# Revit family: HUNTER_PROS-04_PRS40
name_source: partatom
category: Sprinklers
revit_build: Autodesk Revit 2017 (Build: 20160225_1515(x64)
units: mm (PartAtom-declared; Revit-internal decimal feet)

## family parameters
Always vertical = Yes
Cut with Voids When Loaded = No
Maintain Annotation Orientation = No
OmniClass Number = 23.11.27.15.11.11
OmniClass Title = Installed Sprinkler Heads
Part Type = Normal
Room Calculation Point = No
Round Connector Dimension = Use Diameter
Shared = Yes
Work Plane-Based = No

## types (19) — shared parameters
Assembly Code = G2050700
Body Height = 155 mm  [stored 0.50853 ft]
Body Material = Hunter® ABS Plastic
Connection_Dia = 15 mm  [stored 0.0492126 ft]
Diameter = 610 mm
Exposed Diameter = 57 mm  [stored 0.187008 ft]
Keynote = 328423.02
Manufacturer = Hunter® Industries
Pop Up Height = 100 mm  [stored 0.328084 ft]
Pop Up Material = Hunter® ABS Plastic
Pressure = 280.0 kPa
Seal = Hunter® White Flex Seal
Trajectory Angle = 25.00°
Type Comments = Pro-Spray® PROS-04
Type Image = <None>
URL = https://www.hunterindustries.com
Water = Water

## per-type parameters (varying)
| type | Arc Max | Arc Min | Description | Inlet Size | MP_Ref_1 | MP_Ref_2 | Model | Nozzle Size | Precipitation Rate | Trajectory Radius | Water Pattern |
| PROS-04-PRS40-CV-MP1000-90_Maroon_4.1m | 210.00° | 90.00° | ProSpray® with Pressure Regulator PROS-04-PRS40 10cm PopUp and MP Rotator MP1000-90 | 1/2'' NPT | 1000 | 90 | PROS-04-PRS40-CV-MP1000-90 | Hunter®MP Rotator (MP1000) Maroon Nozzle | 11 mm/hr | 4100 mm  [stored 13.4514 ft] | Water Arc |
| PROS-04-PRS40-CV-MP1000-360_Olive_4.1m | 360.00° | 360.00° | ProSpray® with Pressure Regulator PROS-04-PRS40 10cm PopUp and MP Rotator MP1000-360 | 1/2" NPT | 1000 | 360 | PROS-04-PRS40-CV-MP1000-360 | Hunter®MP Rotator (MP1000) Olive Nozzle | 11 mm/hr | 4100 mm  [stored 13.4514 ft] | Water Arc |
| PROS-04-PRS40-CV-MP1000-210_Lt.Blue_4.1m | 270.00° | 210.00° | ProSpray® with Pressure Regulator PROS-04-PRS40 10cm PopUp and MP Rotator MP1000-210 | 1/2" NPT | 1000 | 210 | PROS-04-PRS40-CV-MP1000-210 | Hunter® MP Rotator (MP1000) Lt.Blue Nozzle | 11 mm/hr | 4100 mm  [stored 13.4514 ft] | Water Arc |
| PROS-04-PRS40-CV-MP2000-210_Green_5.8 m | 270.00° | 210.00° | ProSpray® with Pressure Regulator PROS-04-PRS40 10cm PopUp and MP Rotator MP2000-210 | 1/2" NPT | 2000 | 210 | PROS-04-PRS40-CV-MP2000-210 | Hunter® MP Rotator (MP2000) Green Nozzle | 10 mm/hr | 5800 mm  [stored 19.0289 ft] | Water Arc |
| PROS-04-PRS40-CV-MP2000-90_Black_5.8m | 210.00° | 90.00° | ProSpray® with Pressure Regulator PROS-04-PRS40 10cm PopUp and MP Rotator MP2000-90 | 1/2'' NPT | 2000 | 90 | PROS-04-PRS40-CV-MP2000-90 | Hunter® MP Rotator (MP2000) Black Nozzle | 11 mm/hr | 5800 mm  [stored 19.0289 ft] | Water Arc |
| PROS-04-PRS40-CV-MP2000-360_Red_5.8m | 360.00° | 360.00° | ProSpray® with Pressure Regulator PROS-04-PRS40 10cm PopUp and MP Rotator MP2000-360 | 1/2" NPT | 2000 | 360 | PROS-04-PRS40-CV-MP2000-360 | Hunter® MP Rotator (MP2000) Red Nozzle | 10 mm/hr | 5800 mm  [stored 19.0289 ft] | Water Arc |
| PROS-04-PRS40-CV-MP3000-210_Yellow_9.1m | 270.00° | 210.00° | ProSpray® with Pressure Regulator PROS-04-PRS40 10cm PopUp and MP Rotator MP3000-210 | 1/2'' NPT | 3000 | 210 | PROS-04-PRS40-CV-MP3000-210 | Hunter® MP Rotator (MP3000) Yellow Nozzle | 10 mm/hr | 9100 mm  [stored 29.8556 ft] | Water Arc |
| PROS-04-PRS40-CV-MP3000-360_Grey_9.1m | 360.00° | 360.00° | ProSpray® with Pressure Regulator PROS-04-PRS40 10cm PopUp and MP Rotator MP3000-360 | 1/2" NPT | 3000 | 360 | PROS-04-PRS40-CV-MP3000-360 | Hunter® MP Rotator (MP3000) Grey Nozzle | 10 mm/hr | 9100 mm  [stored 29.8556 ft] | Water Arc |
| PROS-04-PRS40-CV-MP3000-90_Blue_9.1m | 210.00° | 90.00° | ProSpray® with Pressure Regulator PROS-04-PRS40 10cm PopUp and MP Rotator MP3000-90 | 1/2'' NPT | 3000 | 90 | PROS-04-PRS40-CV-MP3000-90 | Hunter® MP Rotator (MP3000) Blue Nozzle | 10 mm/hr | 9100 mm  [stored 29.8556 ft] | Water Arc |
| PROS-04-PRS40-CV-MPCorner_Turquoise-4.1m | 105.00° | 45.00° | ProSpray® with Pressure Regulator PROS-04-PRS40 10cm PopUp and MP Rotator MPCorner | 1/2'' NPT | 4000 | 45 | PROS-04-PRS40-CV-MPCorner | Hunter® MP Rotator (MPCorner) Turquoise Nozzle | 11 mm/hr | 4100 mm  [stored 13.4514 ft] | Water Arc |
| PROS-04-PRS40-CV-MP3500-90_Light Brown_10.7m | 210.00° | 90.00° | ProSpray® with Pressure Regulator PROS-04-PRS40 10cm PopUp and MP Rotator MP3500-90 | 1/2'' NPT | 3500 | 90 | PROS-04-PRS40-CV-MP3500-90 | Hunter® MP Rotator (MP3500) Light Brown Nozzle | 11 mm/hr | 10700 mm  [stored 35.105 ft] | Water Arc |
| PROS-04-PRS40-CV-MPLCS-515_Ivory_1.5x4.6m | 1.00° | 1.00° | ProSpray® with Pressure Regulator PROS-04-PRS40 10cm PopUp and MP Rotator MPLCS-515 | 1/2'' NPT | 515 | 1 | PROS-04-PRS40-CV-MPLCS-515 | Hunter® MP Rotator (MPLCS-515) Ivory Nozzle | 11 mm/hr | 1 mm  [stored 0.00328084 ft] | Water Left Strip |
| PROS-04-PRS40-CV-MPRCS-515_Copper_1.5x4.6m | 1.00° | 1.00° | ProSpray® with Pressure Regulator PROS-04-PRS40 10cm PopUp and MP Rotator MPRCS-515 | 1/2'' NPT | 515 | 1 | PROS-04-PRS40-CV-MPRCS-515 | Hunter® MP Rotator (MPRCS-515) Copper Nozzle | 11 mm/hr | 1 mm  [stored 0.00328084 ft] | Water Right Strip |
| PROS-04-PRS40-CV-MPSS-530_Brown_1.5x9.1m | 1.00° | 1.00° | ProSpray® with Pressure Regulator PROS-04-PRS40 10cm PopUp and MP Rotator MPSS-530 | 1/2'' NPT | 530 | 1 | PROS-04-PRS40-CV-MPSS-530 | Hunter® MP Rotator (MPSS-530) Brown Nozzle | 11 mm/hr | 1 mm  [stored 0.00328084 ft] | Water Side Strip |
| PROS-04-PRS40-CV-MP800SR-90_Orange and Grey_3.0m | 210.00° | 90.00° | ProSpray® with Pressure Regulator PROS-04-PRS40 10cm PopUp and MP800 Series MP800SR-90 | 1/2'' NPT | 800 | 90 | PROS-04-PRS40-CV-MP800SR-90 | Hunter®MP Rotator (MP1800SR) Orange and Grey Nozzle | 21 mm/hr | 3000 mm  [stored 9.84252 ft] | Water Arc |
| PROS-04-PRS40-CV-MP800SR-360_Lime Green and Grey_3.0m | 360.00° | 360.00° | ProSpray® with Pressure Regulator PROS-04-PRS40 10cm PopUp and MP800 Series Rotator MP800SR-360 | 1/2" NPT | 800 | 360 | PROS-04-PRS40-CV-MP800SR-360 | Hunter®MP Rotator (MP800SR) Lime Green and Grey Nozzle | 20 mm/hr | 3000 mm  [stored 9.84252 ft] | Water Arc |
| PROS-04-PRS40-CV-MP815-360_Olive and Grey_4.5m | 360.00° | 360.00° | ProSpray® with Pressure Regulator PROS-04-PRS40 10cm PopUp and MP800 Series MP815-360 | 1/2" NPT | 815 | 360 | PROS-04-PRS40-CV-MP815-360 | Hunter®MP Rotator (MP815) Olive and Grey Nozzle | 21 mm/hr | 4500 mm | Water Arc |
| PROS-04-PRS40-CV-MP815-90_Maroon and Grey_4.5m | 210.00° | 90.00° | ProSpray® with Pressure Regulator PROS-04-PRS40 10cm PopUp and MP800 Series MP815-90 | 1/2'' NPT | 815 | 90 | PROS-04-PRS40-CV-MP815-90 | Hunter®MP Rotator (MP815) Maroon and Grey Nozzle | 21 mm/hr | 4500 mm | Water Arc |
| PROS-04-PRS40-CV-MP815-210_Lt. Blue and Grey_4.5m | 270.00° | 210.00° | ProSpray® with Pressure Regulator PROS-04-PRS40 10cm PopUp and MP800 Series MP815-210 | 1/2" NPT | 815 | 210 | PROS-04-PRS40-CV-MP815-210 | Hunter® MP Rotator (MP815) Lt.Blue and Grey Nozzle | 21 mm/hr | 4500 mm | Water Arc |

note: [stored X ft] marks values corroborated as IEEE doubles in the binary element streams (Revit-internal decimal feet)

## geometry (parser evidence)
native form markers: Sweep x44
no freeform markers — native parametric forms only
